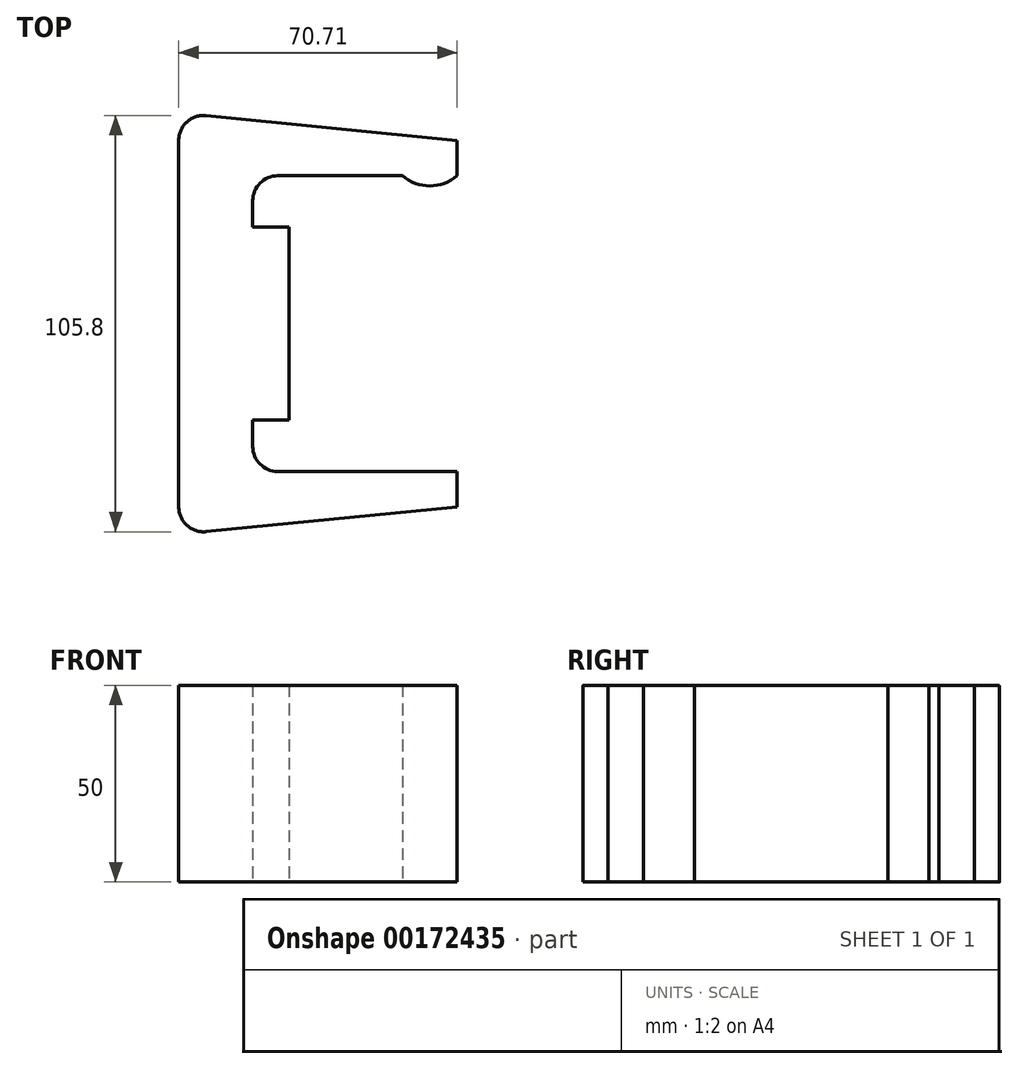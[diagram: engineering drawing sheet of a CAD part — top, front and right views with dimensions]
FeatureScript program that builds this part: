
annotation { "Feature Type Name" : "Feature", "Feature Type Description" : "" }
export const myFeature = defineFeature(function(context is Context, id is Id, definition is map)
    precondition{}
    {
        {
            var Q0;
            Q0=qCreatedBy(makeId("Top.planeOp"),FACE);
            var sketch = newSketch(context, id + "F0", { "sketchPlane" : qUnion([Q0])});
            skLineSegment(sketch, "E0", {"start": v(-28, 0) * mm, "end": v(-28, 46.55) * mm});
            skLineSegment(sketch, "E1", {"start": v(-21.02, 52.87) * mm, "end": v(42.7, 46.55) * mm});
            skLineSegment(sketch, "E2", {"start": v(42.7, 46.55) * mm, "end": v(42.7, 37.55) * mm});
            skLineSegment(sketch, "E3", {"start": v(42.7, 37.55) * mm, "end": v(-2.86, 37.55) * mm});
            skLineSegment(sketch, "E4", {"start": v(-9.2, 31.2) * mm, "end": v(-9.2, 24.55) * mm});
            skLineSegment(sketch, "E5", {"start": v(-9.2, 24.55) * mm, "end": v(0, 24.55) * mm});
            skLineSegment(sketch, "E6", {"start": v(0, 24.55) * mm, "end": v(0, 0) * mm});
            skLineSegment(sketch, "E7", {"start": v(28.86, 72.3) * mm, "end": v(28.86, 48.01) * mm, "construction": true});
            skArc(sketch, "E8", {"start": v(28.86, 37.55) * mm, "mid": v(35.78, 35) * mm, "end": v(42.7, 37.55) * mm});
            skPoint(sketch, "E9.visualSharp", {"position": v(-9.2, 37.55) * mm});
            skArc(sketch, "E9.filletArc", {"start": v(-2.86, 37.55) * mm, "mid": v(-7.35, 35.7) * mm, "end": v(-9.2, 31.2) * mm});
            skPoint(sketch, "E10.visualSharp", {"position": v(-28, 53.56) * mm});
            skArc(sketch, "E10.filletArc", {"start": v(-21.02, 52.87) * mm, "mid": v(-25.91, 51.26) * mm, "end": v(-28, 46.55) * mm});
            skLineSegment(sketch, "E11", {"start": v(-9.2, 24.55) * mm, "end": v(-28, 24.55) * mm});
            skLineSegment(sketch, "E12", {"start": v(42.7, 46.55) * mm, "end": v(-28, 46.55) * mm});
            skLineSegment(sketch, "E13", {"start": v(-28, 0) * mm, "end": v(0, 0) * mm});
            skLineSegment(sketch, "E14.MirrorCS", {"start": v(-9.2, -31.2) * mm, "end": v(-9.2, -24.55) * mm});
            skLineSegment(sketch, "E15.MirrorCS", {"start": v(-9.2, -24.55) * mm, "end": v(0, -24.55) * mm});
            skLineSegment(sketch, "E16.MirrorCS", {"start": v(28.86, -72.3) * mm, "end": v(28.86, -48.01) * mm, "construction": true});
            skArc(sketch, "E17.MirrorCS", {"start": v(28.86, -37.55) * mm, "mid": v(35.78, -35) * mm, "end": v(42.7, -37.55) * mm});
            skArc(sketch, "E18.MirrorCS", {"start": v(-2.86, -37.55) * mm, "mid": v(-7.35, -35.7) * mm, "end": v(-9.2, -31.2) * mm});
            skLineSegment(sketch, "E19.MirrorCS", {"start": v(42.7, -37.55) * mm, "end": v(-2.86, -37.55) * mm});
            skLineSegment(sketch, "E20.MirrorCS", {"start": v(-21.02, -52.87) * mm, "end": v(42.7, -46.55) * mm});
            skLineSegment(sketch, "E21.MirrorCS", {"start": v(-9.2, -24.55) * mm, "end": v(-28, -24.55) * mm});
            skArc(sketch, "E22.MirrorCS", {"start": v(-21.02, -52.87) * mm, "mid": v(-25.91, -51.26) * mm, "end": v(-28, -46.55) * mm});
            skPoint(sketch, "E23.MirrorP", {"position": v(-28, -53.56) * mm});
            skLineSegment(sketch, "E24.MirrorCS", {"start": v(42.7, -46.55) * mm, "end": v(-28, -46.55) * mm});
            skPoint(sketch, "E25.MirrorP", {"position": v(-9.2, -37.55) * mm});
            skLineSegment(sketch, "E26.MirrorCS", {"start": v(42.7, -46.55) * mm, "end": v(42.7, -37.55) * mm});
            skLineSegment(sketch, "E27.MirrorCS", {"start": v(-28, 0) * mm, "end": v(-28, -46.55) * mm});
            skLineSegment(sketch, "E28.MirrorCS", {"start": v(0, -24.55) * mm, "end": v(0, 0) * mm});
            skSolve(sketch);
        }
        {
            var Q0;
            Q0=makeQuery(id+"F0.imprint","IMPRINT",FACE,{"disambiguationData":[TD([[makeQuery(id+"F0.imprint","IMPRINT",EDGE,{"derivedFrom":sQuery(id+"F0.wireOp",EDGE,"E0")}),-1.0]])]});
            var Q1;
            {var subQ1=sQuery(id+"F0.wireOp",EDGE,"bb5eaa92-9002-4a6b-8970-26d1b829d28c0.MirrorCS");Q1=makeQuery(id+"F0.imprint","IMPRINT",FACE,{"disambiguationData":[TD([[makeQuery(id+"F0.imprint","IMPRINT",EDGE,{"derivedFrom":subQ1}),1.0]])]});}
            var Q2;
            {var subQ0=sQuery(id+"F0.wireOp",EDGE,"E8");Q2=makeQuery(id+"F0.imprint","IMPRINT",FACE,{"disambiguationData":[TD([[makeQuery(id+"F0.imprint","IMPRINT",EDGE,{"derivedFrom":subQ0}),1.0]])]});}
            var Q3;
            {var subQ0=sQuery(id+"F0.wireOp",EDGE,"bb5eaa92-9002-4a6b-8970-26d1b829d28c6.MirrorCS");Q3=makeQuery(id+"F0.imprint","IMPRINT",FACE,{"disambiguationData":[TD([[makeQuery(id+"F0.imprint","IMPRINT",EDGE,{"derivedFrom":subQ0}),-1.0]])]});}
            var Q4;
            {var subQ5=sQuery(id+"F0.wireOp",EDGE,"E2");Q4=makeQuery(id+"F0.imprint","IMPRINT",FACE,{"disambiguationData":[TD([[makeQuery(id+"F0.imprint","IMPRINT",EDGE,{"derivedFrom":subQ5}),-1.0]])]});}
            var Q5;
            Q5=makeQuery(id+"F0.imprint","IMPRINT",FACE,{"disambiguationData":[TD([[makeQuery(id+"F0.imprint","IMPRINT",EDGE,{"derivedFrom":sQuery(id+"F0.wireOp",EDGE,"E1")}),-1.0]])]});
            var Q6;
            {var subQ1=sQuery(id+"F0.wireOp",EDGE,"e685f284-c3cd-4062-9255-22636a69970a6.MirrorCS");Q6=makeQuery(id+"F0.imprint","IMPRINT",FACE,{"disambiguationData":[TD([[makeQuery(id+"F0.imprint","IMPRINT",EDGE,{"derivedFrom":subQ1}),-1.0]])]});}
            var Q7;
            {var subQ4=sQuery(id+"F0.wireOp",EDGE,"e685f284-c3cd-4062-9255-22636a69970a0.MirrorCS");Q7=makeQuery(id+"F0.imprint","IMPRINT",FACE,{"disambiguationData":[TD([[makeQuery(id+"F0.imprint","IMPRINT",EDGE,{"derivedFrom":subQ4}),-1.0]])]});}
            var Q8;
            Q8=makeQuery(id+"F0.imprint","IMPRINT",FACE,{"disambiguationData":[TD([[makeQuery(id+"F0.imprint","IMPRINT",EDGE,{"derivedFrom":sQuery(id+"F0.wireOp",EDGE,"e685f284-c3cd-4062-9255-22636a69970a0.MirrorCS")}),1.0]])]});
            var Q9;
            {var subQ0=sQuery(id+"F0.wireOp",EDGE,"e685f284-c3cd-4062-9255-22636a69970a12.MirrorCS");Q9=makeQuery(id+"F0.imprint","IMPRINT",FACE,{"disambiguationData":[TD([[makeQuery(id+"F0.imprint","IMPRINT",EDGE,{"derivedFrom":subQ0}),-1.0]])]});}
            var Q10;
            {var subQ1=sQuery(id+"F0.wireOp",EDGE,"E13");Q10=makeQuery(id+"F0.imprint","IMPRINT",FACE,{"disambiguationData":[TD([[makeQuery(id+"F0.imprint","IMPRINT",EDGE,{"derivedFrom":subQ1}),-1.0]])]});}
            var Q11;
            Q11=makeQuery(id+"F0.imprint","IMPRINT",FACE,{"disambiguationData":[TD([[makeQuery(id+"F0.imprint","IMPRINT",EDGE,{"derivedFrom":sQuery(id+"F0.wireOp",EDGE,"E14.MirrorCS")}),1.0]])]});
            var Q12;
            Q12=makeQuery(id+"F0.imprint","IMPRINT",FACE,{"disambiguationData":[TD([[makeQuery(id+"F0.imprint","IMPRINT",EDGE,{"derivedFrom":sQuery(id+"F0.wireOp",EDGE,"E20.MirrorCS")}),1.0]])]});
            var Q13;
            {var subQ0=sQuery(id+"F0.wireOp",EDGE,"E17.MirrorCS");Q13=makeQuery(id+"F0.imprint","IMPRINT",FACE,{"disambiguationData":[TD([[makeQuery(id+"F0.imprint","IMPRINT",EDGE,{"derivedFrom":subQ0}),-1.0]])]});}
            extrude(context, id + "F1", {"entities" : qUnion([Q0, Q1, Q2, Q3, Q4, Q5, Q6, Q7, Q8, Q9, Q10, Q11, Q12, Q13]), "depth" : 50 * mm});
        }
    });
